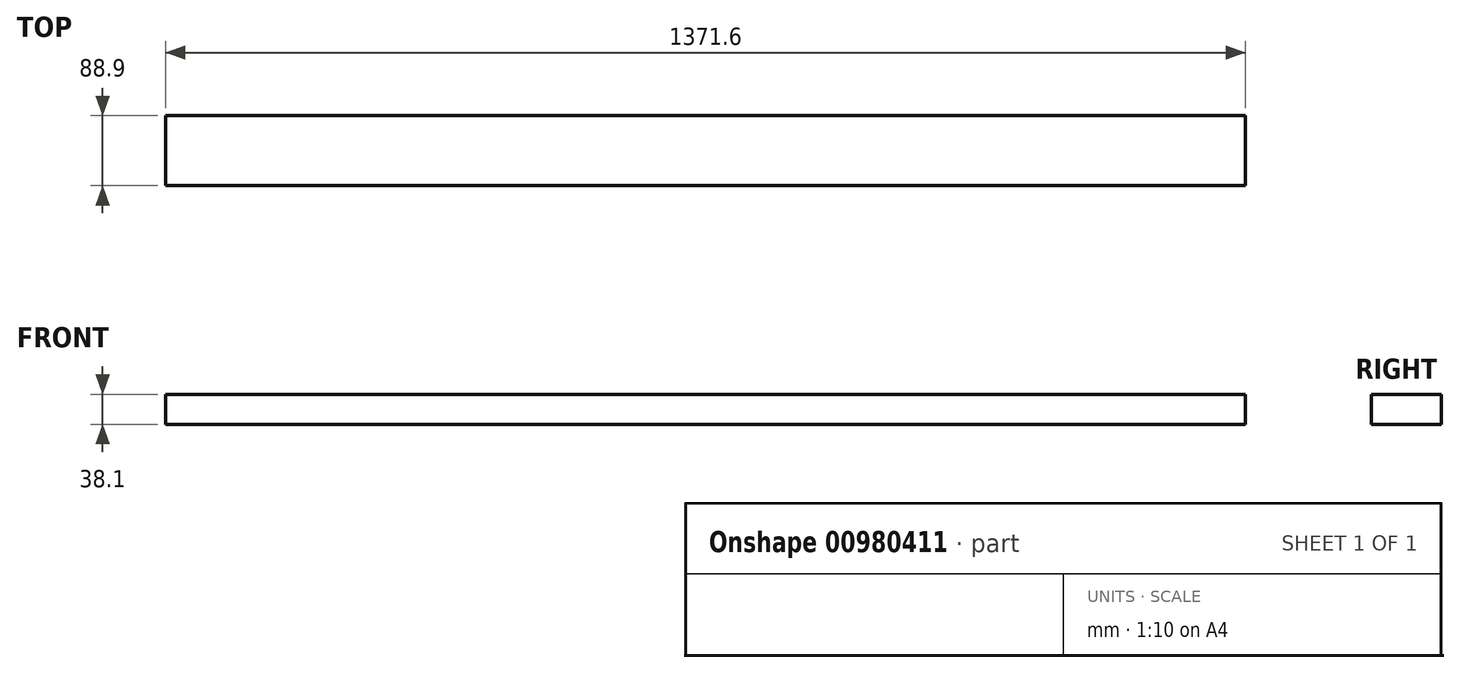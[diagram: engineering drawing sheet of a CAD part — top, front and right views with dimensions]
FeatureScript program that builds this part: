
annotation { "Feature Type Name" : "Feature", "Feature Type Description" : "" }
export const myFeature = defineFeature(function(context is Context, id is Id, definition is map)
    precondition{}
    {
        {
            var Q0;
            Q0=qCreatedBy(makeId("Right.planeOp"),FACE);
            var sketch = newSketch(context, id + "F0", { "sketchPlane" : qUnion([Q0])});
            skLineSegment(sketch, "E0.bottom", {"start": v(44.45, -19.05) * mm, "end": v(-44.45, -19.05) * mm});
            skLineSegment(sketch, "E0.top", {"start": v(44.45, 19.05) * mm, "end": v(-44.45, 19.05) * mm});
            skLineSegment(sketch, "E0.left", {"start": v(44.45, -19.05) * mm, "end": v(44.45, 19.05) * mm});
            skLineSegment(sketch, "E0.right", {"start": v(-44.45, -19.05) * mm, "end": v(-44.45, 19.05) * mm});
            skPoint(sketch, "E0.middle", {"position": v(0, 0) * mm});
            skSolve(sketch);
        }
        {
            var Q0;
            Q0=qSketchRegion(id+"F0",true);
            var Q1;
            Q1=makeQuery(id+"F0.imprint","IMPRINT",FACE,{"disambiguationData":[TD([[makeQuery(id+"F0.imprint","IMPRINT",EDGE,{"derivedFrom":sQuery(id+"F0.wireOp",EDGE,"E0.bottom")}),-1.0]])]});
            extrude(context, id + "F1", {"entities" : qUnion([Q0, Q1]), "depth" : 1371.6 * mm, "offsetDistance" : 25.4 * mm});
        }
    });
